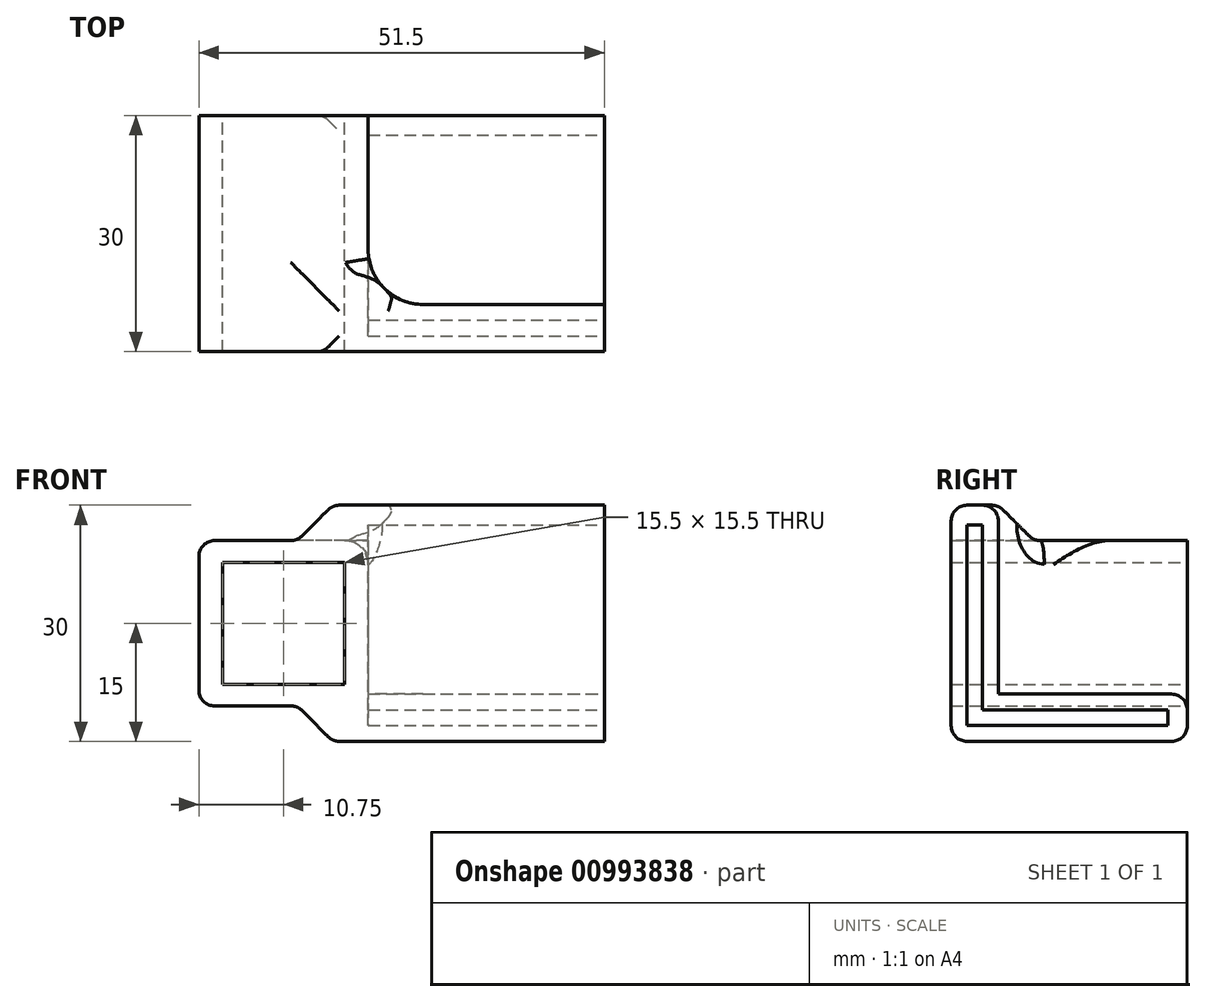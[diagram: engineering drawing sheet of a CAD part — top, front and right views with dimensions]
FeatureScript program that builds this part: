
annotation { "Feature Type Name" : "Feature", "Feature Type Description" : "" }
export const myFeature = defineFeature(function(context is Context, id is Id, definition is map)
    precondition{}
    {
        {
            var Q0;
            Q0=qCreatedBy(makeId("Top.planeOp"),FACE);
            var sketch = newSketch(context, id + "F0", { "sketchPlane" : qUnion([Q0])});
            skLineSegment(sketch, "E0", {"start": v(18, -44.27) * mm, "end": v(24, -44.27) * mm});
            skLineSegment(sketch, "E1", {"start": v(24, -44.27) * mm, "end": v(24, -14.27) * mm});
            skLineSegment(sketch, "E2", {"start": v(24, -14.27) * mm, "end": v(-12, -14.27) * mm});
            skLineSegment(sketch, "E3", {"start": v(-12, -14.27) * mm, "end": v(-12, -44.27) * mm});
            skLineSegment(sketch, "E4", {"start": v(-6, -44.27) * mm, "end": v(-6, -20.27) * mm});
            skLineSegment(sketch, "E5", {"start": v(-6, -20.27) * mm, "end": v(24, -20.27) * mm});
            skLineSegment(sketch, "E6", {"start": v(18, -44.27) * mm, "end": v(-12, -44.27) * mm});
            skSolve(sketch);
        }
        {
            var Q0;
            {var subQ2=sQuery(id+"F0.wireOp",EDGE,"E0");Q0=makeQuery(id+"F0.imprint","IMPRINT",FACE,{"disambiguationData":[TD([[makeQuery(id+"F0.imprint","IMPRINT",EDGE,{"derivedFrom":subQ2}),1.0]])]});}
            extrude(context, id + "F1", {"entities" : qUnion([Q0]), "depth" : 6 * mm, "offsetDistance" : 25 * mm});
        }
        {
            var Q0;
            {var subQ1=sQuery(id+"F0.wireOp",EDGE,"E2");Q0=makeQuery(id+"F0.imprint","IMPRINT",FACE,{"disambiguationData":[TD([[makeQuery(id+"F0.imprint","IMPRINT",EDGE,{"derivedFrom":subQ1}),1.0]])]});}
            extrude(context, id + "F2", {"entities" : qUnion([Q0]), "operationType" : NewBodyOperationType.ADD, "depth" : 30 * mm, "offsetDistance" : 25 * mm});
        }
        {
            var Q0;
            {var subQ0=sQuery(id+"F0.wireOp",EDGE,"E1");Q0=makeQuery(id+"F2.boolean.opBoolean","MERGE",FACE,{"derivedFrom":[makeQuery(id+"F1.opExtrude","SWEPT_FACE",FACE,{"disambiguationData":[OSD([subQ0])]}),makeQuery(id+"F2.opExtrude","SWEPT_FACE",FACE,{"disambiguationData":[OSD([subQ0])]})]});}
            var sketch = newSketch(context, id + "F3", { "sketchPlane" : qUnion([Q0])});
            skLineSegment(sketch, "E7", {"start": v(-41.77, 4) * mm, "end": v(-18.27, 4) * mm});
            skLineSegment(sketch, "E8", {"start": v(-18.27, 4) * mm, "end": v(-18.27, 27.5) * mm});
            skLineSegment(sketch, "E9", {"start": v(-18.27, 27.5) * mm, "end": v(-16.27, 27.5) * mm});
            skLineSegment(sketch, "E10", {"start": v(-16.27, 27.5) * mm, "end": v(-16.27, 2) * mm});
            skLineSegment(sketch, "E11", {"start": v(-16.27, 2) * mm, "end": v(-41.77, 2) * mm});
            skLineSegment(sketch, "E12", {"start": v(-41.77, 2) * mm, "end": v(-41.77, 4) * mm});
            skSolve(sketch);
        }
        {
            var Q0;
            Q0=makeQuery(id+"F3.imprint","IMPRINT",FACE,{"disambiguationData":[TD([[makeQuery(id+"F3.imprint","IMPRINT",EDGE,{"derivedFrom":sQuery(id+"F3.wireOp",EDGE,"E7")}),-1.0]])]});
            extrude(context, id + "F4", {"entities" : qUnion([Q0]), "operationType" : NewBodyOperationType.REMOVE, "oppositeDirection" : true, "depth" : 30 * mm, "offsetDistance" : 25 * mm});
        }
        {
            var Q0;
            Q0=makeQuery(id+"F2.opExtrude","SWEPT_FACE",FACE,{"disambiguationData":[OSD([sQuery(id+"F0.wireOp",EDGE,"E3")])]});
            extrude(context, id + "F5", {"entities" : qUnion([Q0]), "operationType" : NewBodyOperationType.ADD, "depth" : 20 * mm, "offsetDistance" : 25 * mm});
        }
        {
            var Q0;
            {var subQ0=sQuery(id+"F0.wireOp",EDGE,"E6");Q0=makeQuery(id+"F5.boolean.opBoolean","MERGE",FACE,{"derivedFrom":[makeQuery(id+"F2.boolean.opBoolean","MERGE",FACE,{"derivedFrom":[makeQuery(id+"F1.opExtrude","SWEPT_FACE",FACE,{"disambiguationData":[OSD([sQuery(id+"F0.wireOp",EDGE,"E0"),subQ0])]}),makeQuery(id+"F2.opExtrude","SWEPT_FACE",FACE,{"disambiguationData":[OSD([subQ0])]})]}),makeQuery(id+"F5.opExtrude","SWEPT_FACE",FACE,{"disambiguationData":[OSD([sQuery(id+"F0.wireOp",EDGE,"E3"),subQ0])]})]});}
            var sketch = newSketch(context, id + "F6", { "sketchPlane" : qUnion([Q0])});
            skLineSegment(sketch, "E13.bottom", {"start": v(-9, 7.25) * mm, "end": v(-24.5, 7.25) * mm});
            skLineSegment(sketch, "E13.top", {"start": v(-9, 22.75) * mm, "end": v(-24.5, 22.75) * mm});
            skLineSegment(sketch, "E13.left", {"start": v(-9, 7.25) * mm, "end": v(-9, 22.75) * mm});
            skLineSegment(sketch, "E13.right", {"start": v(-24.5, 7.25) * mm, "end": v(-24.5, 22.75) * mm});
            skPoint(sketch, "E13.middle", {"position": v(-16.75, 15) * mm});
            skLineSegment(sketch, "E14", {"start": v(-10.5, 25.5) * mm, "end": v(-10.5, 30) * mm});
            skLineSegment(sketch, "E15", {"start": v(-10.5, 25.5) * mm, "end": v(-27.5, 25.5) * mm});
            skLineSegment(sketch, "E16", {"start": v(-27.5, 25.5) * mm, "end": v(-27.5, 4.5) * mm});
            skLineSegment(sketch, "E17", {"start": v(-27.5, 4.5) * mm, "end": v(-10.5, 4.5) * mm});
            skLineSegment(sketch, "E18", {"start": v(-10.5, 4.5) * mm, "end": v(-10.5, 0) * mm});
            skLineSegment(sketch, "E19", {"start": v(-10.5, 0) * mm, "end": v(-32, 0) * mm});
            skLineSegment(sketch, "E20", {"start": v(-32, 0) * mm, "end": v(-32, 30) * mm});
            skLineSegment(sketch, "E21", {"start": v(-32, 30) * mm, "end": v(-10.5, 30) * mm});
            skLineSegment(sketch, "E22", {"start": v(-10.5, 25.5) * mm, "end": v(-6, 25.5) * mm});
            skLineSegment(sketch, "E23", {"start": v(-6, 25.5) * mm, "end": v(-6, 30) * mm});
            skLineSegment(sketch, "E24", {"start": v(-6, 30) * mm, "end": v(-10.5, 30) * mm});
            skSolve(sketch);
        }
        {
            var Q0;
            Q0=makeQuery(id+"F6.imprint","IMPRINT",FACE,{"disambiguationData":[TD([[makeQuery(id+"F6.imprint","IMPRINT",EDGE,{"derivedFrom":sQuery(id+"F6.wireOp",EDGE,"E13.bottom")}),-1.0]])]});
            var Q1;
            {var subQ0=sQuery(id+"F0.wireOp",EDGE,"E2");Q1=makeQuery(id+"F5.boolean.opBoolean","MERGE",FACE,{"derivedFrom":[makeQuery(id+"F2.opExtrude","SWEPT_FACE",FACE,{"disambiguationData":[OSD([subQ0])]}),makeQuery(id+"F5.opExtrude","SWEPT_FACE",FACE,{"disambiguationData":[OSD([subQ0,sQuery(id+"F0.wireOp",EDGE,"E3")])]})]});}
            extrude(context, id + "F7", {"entities" : qUnion([Q0]), "operationType" : NewBodyOperationType.REMOVE, "endBound" : BoundingType.UP_TO_SURFACE, "oppositeDirection" : true, "depth" : 25 * mm, "endBoundEntityFace" : qUnion([Q1]), "offsetDistance" : 25 * mm});
        }
        {
            var Q0;
            Q0=makeQuery(id+"F6.imprint","IMPRINT",FACE,{"disambiguationData":[TD([[makeQuery(id+"F6.imprint","IMPRINT",EDGE,{"derivedFrom":sQuery(id+"F6.wireOp",EDGE,"E14")}),1.0]])]});
            var Q1;
            {var subQ0=sQuery(id+"F0.wireOp",EDGE,"E2");Q1=makeQuery(id+"F5.boolean.opBoolean","MERGE",FACE,{"derivedFrom":[makeQuery(id+"F2.opExtrude","SWEPT_FACE",FACE,{"disambiguationData":[OSD([subQ0])]}),makeQuery(id+"F5.opExtrude","SWEPT_FACE",FACE,{"disambiguationData":[OSD([subQ0,sQuery(id+"F0.wireOp",EDGE,"E3")])]})]});}
            extrude(context, id + "F8", {"entities" : qUnion([Q0]), "operationType" : NewBodyOperationType.REMOVE, "endBound" : BoundingType.UP_TO_SURFACE, "oppositeDirection" : true, "depth" : 25 * mm, "endBoundEntityFace" : qUnion([Q1]), "offsetDistance" : 25 * mm});
        }
        {
            var Q0;
            Q0=makeQuery(id+"F6.imprint","IMPRINT",FACE,{"disambiguationData":[TD([[makeQuery(id+"F6.imprint","IMPRINT",EDGE,{"derivedFrom":sQuery(id+"F6.wireOp",EDGE,"E14")}),-1.0]])]});
            var Q1;
            Q1=makeQuery(id+"F2.opExtrude","SWEPT_FACE",FACE,{"disambiguationData":[OSD([sQuery(id+"F0.wireOp",EDGE,"E5")])]});
            extrude(context, id + "F9", {"entities" : qUnion([Q0]), "operationType" : NewBodyOperationType.REMOVE, "endBound" : BoundingType.UP_TO_SURFACE, "oppositeDirection" : true, "depth" : 22 * mm, "endBoundEntityFace" : qUnion([Q1]), "offsetDistance" : 25 * mm});
        }
        {
            var Q0;
            Q0=makeQuery(id+"F8.boolean.opBoolean","COPY",EDGE,{"derivedFrom":makeQuery(id+"F8.opExtrude","SWEPT_EDGE",EDGE,{"disambiguationData":[OSD([sQuery(id+"F6.wireOp",EDGE,"E14"),sQuery(id+"F6.wireOp",EDGE,"E15"),sQuery(id+"F6.wireOp",EDGE,"E22")])]})});
            var Q1;
            Q1=makeQuery(id+"F8.boolean.opBoolean","COPY",EDGE,{"derivedFrom":makeQuery(id+"F8.opExtrude","SWEPT_EDGE",EDGE,{"disambiguationData":[OSD([sQuery(id+"F6.wireOp",EDGE,"E17"),sQuery(id+"F6.wireOp",EDGE,"E18")])]})});
            var Q2;
            Q2=makeQuery(id+"F9.boolean.opBoolean","COPY",EDGE,{"derivedFrom":makeQuery(id+"F9.opExtrude","CAP_EDGE",EDGE,{"disambiguationData":[OSD([sQuery(id+"F6.wireOp",EDGE,"E22")])],"isStart":false})});
            chamfer(context, id + "F10", {"entities" : qUnion([Q0, Q1, Q2]), "width" : 4.5 * mm, "tangentPropagation" : true});
        }
        {
            var Q0;
            Q0=makeQuery(id+"F2.opExtrude","SWEPT_EDGE",EDGE,{"disambiguationData":[OSD([sQuery(id+"F0.wireOp",EDGE,"E4"),sQuery(id+"F0.wireOp",EDGE,"E5")])]});
            var Q1;
            Q1=makeQuery(id+"F1.opExtrude","CAP_EDGE",EDGE,{"disambiguationData":[OSD([sQuery(id+"F0.wireOp",EDGE,"E4")])],"isStart":false});
            var Q2;
            Q2=makeQuery(id+"F1.opExtrude","CAP_EDGE",EDGE,{"disambiguationData":[OSD([sQuery(id+"F0.wireOp",EDGE,"E5")])],"isStart":false});
            fillet(context, id + "F11", {"entities" : qUnion([Q0, Q1, Q2]), "radius" : 7 * mm, "tangentPropagation" : true, "allowEdgeOverflow" : false});
        }
        {
            var Q0;
            {var subQ0=sQuery(id+"F6.wireOp",EDGE,"E22");var subQ1=sQuery(id+"F6.wireOp",EDGE,"E15");Q0=makeQuery(id+"F10.opChamfer","BLEND_EDGE",EDGE,{"blendedFrom":[makeQuery(id+"F8.boolean.opBoolean","COPY",EDGE,{"derivedFrom":makeQuery(id+"F8.opExtrude","SWEPT_EDGE",EDGE,{"disambiguationData":[OSD([sQuery(id+"F6.wireOp",EDGE,"E14"),subQ1,subQ0])]})}),makeQuery(id+"F9.boolean.opBoolean","MERGE",FACE,{"derivedFrom":[makeQuery(id+"F8.boolean.opBoolean","COPY",FACE,{"derivedFrom":makeQuery(id+"F8.opExtrude","SWEPT_FACE",FACE,{"disambiguationData":[OSD([subQ1])]})})],"fromTools":[makeQuery(id+"F9.opExtrude","SWEPT_FACE",FACE,{"disambiguationData":[OSD([subQ0])]})]})],"blendedInto":[makeQuery(id+"F9.boolean.opBoolean","MERGE",FACE,{"derivedFrom":[makeQuery(id+"F8.boolean.opBoolean","COPY",FACE,{"derivedFrom":makeQuery(id+"F8.opExtrude","SWEPT_FACE",FACE,{"disambiguationData":[OSD([subQ1])]})})],"fromTools":[makeQuery(id+"F9.opExtrude","SWEPT_FACE",FACE,{"disambiguationData":[OSD([subQ0])]})]})]});}
            var Q1;
            {var subQ0=sQuery(id+"F6.wireOp",EDGE,"E22");Q1=makeQuery(id+"F10.opChamfer","BLEND_EDGE",EDGE,{"blendedFrom":[makeQuery(id+"F9.boolean.opBoolean","COPY",EDGE,{"derivedFrom":makeQuery(id+"F9.opExtrude","CAP_EDGE",EDGE,{"disambiguationData":[OSD([subQ0])],"isStart":false})}),makeQuery(id+"F9.boolean.opBoolean","MERGE",FACE,{"derivedFrom":[makeQuery(id+"F8.boolean.opBoolean","COPY",FACE,{"derivedFrom":makeQuery(id+"F8.opExtrude","SWEPT_FACE",FACE,{"disambiguationData":[OSD([sQuery(id+"F6.wireOp",EDGE,"E15")])]})})],"fromTools":[makeQuery(id+"F9.opExtrude","SWEPT_FACE",FACE,{"disambiguationData":[OSD([subQ0])]})]})],"blendedInto":[makeQuery(id+"F9.boolean.opBoolean","MERGE",FACE,{"derivedFrom":[makeQuery(id+"F8.boolean.opBoolean","COPY",FACE,{"derivedFrom":makeQuery(id+"F8.opExtrude","SWEPT_FACE",FACE,{"disambiguationData":[OSD([sQuery(id+"F6.wireOp",EDGE,"E15")])]})})],"fromTools":[makeQuery(id+"F9.opExtrude","SWEPT_FACE",FACE,{"disambiguationData":[OSD([subQ0])]})]})]});}
            var Q2;
            {var subQ0=sQuery(id+"F0.wireOp",EDGE,"E3");Q2=makeQuery(id+"F10.opChamfer","BLEND_EDGE",EDGE,{"blendedFrom":[makeQuery(id+"F9.boolean.opBoolean","COPY",EDGE,{"derivedFrom":makeQuery(id+"F9.opExtrude","CAP_EDGE",EDGE,{"disambiguationData":[OSD([sQuery(id+"F6.wireOp",EDGE,"E22")])],"isStart":false})}),makeQuery(id+"F5.boolean.opBoolean","MERGE",FACE,{"derivedFrom":[makeQuery(id+"F2.opExtrude","CAP_FACE",FACE,{"disambiguationData":[OSD([sQuery(id+"F0.wireOp",EDGE,"E1"),sQuery(id+"F0.wireOp",EDGE,"E2"),subQ0,sQuery(id+"F0.wireOp",EDGE,"E4"),sQuery(id+"F0.wireOp",EDGE,"E5"),sQuery(id+"F0.wireOp",EDGE,"E6")])],"isStart":false}),makeQuery(id+"F5.opExtrude","SWEPT_FACE",FACE,{"disambiguationData":[OSD([subQ0]),TDD([makeQuery(id+"F2.opExtrude","CAP_EDGE",EDGE,{"disambiguationData":[OSD([subQ0])],"isStart":false})])]})]})],"blendedInto":[makeQuery(id+"F5.boolean.opBoolean","MERGE",FACE,{"derivedFrom":[makeQuery(id+"F2.opExtrude","CAP_FACE",FACE,{"disambiguationData":[OSD([sQuery(id+"F0.wireOp",EDGE,"E1"),sQuery(id+"F0.wireOp",EDGE,"E2"),subQ0,sQuery(id+"F0.wireOp",EDGE,"E4"),sQuery(id+"F0.wireOp",EDGE,"E5"),sQuery(id+"F0.wireOp",EDGE,"E6")])],"isStart":false}),makeQuery(id+"F5.opExtrude","SWEPT_FACE",FACE,{"disambiguationData":[OSD([subQ0]),TDD([makeQuery(id+"F2.opExtrude","CAP_EDGE",EDGE,{"disambiguationData":[OSD([subQ0])],"isStart":false})])]})]})]});}
            var Q3;
            {var subQ0=sQuery(id+"F0.wireOp",EDGE,"E3");Q3=makeQuery(id+"F10.opChamfer","BLEND_EDGE",EDGE,{"blendedFrom":[makeQuery(id+"F8.boolean.opBoolean","COPY",EDGE,{"derivedFrom":makeQuery(id+"F8.opExtrude","SWEPT_EDGE",EDGE,{"disambiguationData":[OSD([sQuery(id+"F6.wireOp",EDGE,"E14"),sQuery(id+"F6.wireOp",EDGE,"E15"),sQuery(id+"F6.wireOp",EDGE,"E22")])]})}),makeQuery(id+"F5.boolean.opBoolean","MERGE",FACE,{"derivedFrom":[makeQuery(id+"F2.opExtrude","CAP_FACE",FACE,{"disambiguationData":[OSD([sQuery(id+"F0.wireOp",EDGE,"E1"),sQuery(id+"F0.wireOp",EDGE,"E2"),subQ0,sQuery(id+"F0.wireOp",EDGE,"E4"),sQuery(id+"F0.wireOp",EDGE,"E5"),sQuery(id+"F0.wireOp",EDGE,"E6")])],"isStart":false}),makeQuery(id+"F5.opExtrude","SWEPT_FACE",FACE,{"disambiguationData":[OSD([subQ0]),TDD([makeQuery(id+"F2.opExtrude","CAP_EDGE",EDGE,{"disambiguationData":[OSD([subQ0])],"isStart":false})])]})]})],"blendedInto":[makeQuery(id+"F5.boolean.opBoolean","MERGE",FACE,{"derivedFrom":[makeQuery(id+"F2.opExtrude","CAP_FACE",FACE,{"disambiguationData":[OSD([sQuery(id+"F0.wireOp",EDGE,"E1"),sQuery(id+"F0.wireOp",EDGE,"E2"),subQ0,sQuery(id+"F0.wireOp",EDGE,"E4"),sQuery(id+"F0.wireOp",EDGE,"E5"),sQuery(id+"F0.wireOp",EDGE,"E6")])],"isStart":false}),makeQuery(id+"F5.opExtrude","SWEPT_FACE",FACE,{"disambiguationData":[OSD([subQ0]),TDD([makeQuery(id+"F2.opExtrude","CAP_EDGE",EDGE,{"disambiguationData":[OSD([subQ0])],"isStart":false})])]})]})]});}
            var Q4;
            {var subQ0=sQuery(id+"F0.wireOp",EDGE,"E3");var subQ1=sQuery(id+"F0.wireOp",EDGE,"E2");Q4=makeQuery(id+"F5.boolean.opBoolean","MERGE",EDGE,{"derivedFrom":[makeQuery(id+"F2.opExtrude","CAP_EDGE",EDGE,{"disambiguationData":[OSD([subQ1])],"isStart":false}),makeQuery(id+"F5.opExtrude","SWEPT_EDGE",EDGE,{"disambiguationData":[OSD([subQ1,subQ0]),TDD([makeQuery(id+"F2.opExtrude","CAP_VERTEX",VERTEX,{"disambiguationData":[OSD([subQ1,subQ0])],"isStart":false})])]})]});}
            var Q5;
            Q5=makeQuery(id+"F9.boolean.opBoolean","MERGE",EDGE,{"derivedFrom":[makeQuery(id+"F2.opExtrude","CAP_EDGE",EDGE,{"disambiguationData":[OSD([sQuery(id+"F0.wireOp",EDGE,"E5")])],"isStart":false})],"fromTools":[makeQuery(id+"F9.opExtrude","CAP_EDGE",EDGE,{"disambiguationData":[OSD([sQuery(id+"F6.wireOp",EDGE,"E24")])],"isStart":false})]});
            var Q6;
            Q6=makeQuery(id+"F1.opExtrude","CAP_EDGE",EDGE,{"disambiguationData":[OSD([sQuery(id+"F0.wireOp",EDGE,"E0"),sQuery(id+"F0.wireOp",EDGE,"E6")])],"isStart":false});
            var Q7;
            Q7=makeQuery(id+"F8.boolean.opBoolean","COPY",EDGE,{"derivedFrom":makeQuery(id+"F8.opExtrude","SWEPT_EDGE",EDGE,{"disambiguationData":[OSD([sQuery(id+"F6.wireOp",EDGE,"E15"),sQuery(id+"F6.wireOp",EDGE,"E16")])]})});
            var Q8;
            Q8=makeQuery(id+"F8.boolean.opBoolean","COPY",EDGE,{"derivedFrom":makeQuery(id+"F8.opExtrude","SWEPT_EDGE",EDGE,{"disambiguationData":[OSD([sQuery(id+"F6.wireOp",EDGE,"E16"),sQuery(id+"F6.wireOp",EDGE,"E17")])]})});
            var Q9;
            {var subQ0=sQuery(id+"F0.wireOp",EDGE,"E3");var subQ1=sQuery(id+"F0.wireOp",EDGE,"E2");Q9=makeQuery(id+"F5.boolean.opBoolean","MERGE",EDGE,{"derivedFrom":[makeQuery(id+"F2.opExtrude","CAP_EDGE",EDGE,{"disambiguationData":[OSD([subQ1])],"isStart":true}),makeQuery(id+"F5.opExtrude","SWEPT_EDGE",EDGE,{"disambiguationData":[OSD([subQ1,subQ0]),TDD([makeQuery(id+"F2.opExtrude","CAP_VERTEX",VERTEX,{"disambiguationData":[OSD([subQ1,subQ0])],"isStart":true})])]})]});}
            var Q10;
            {var subQ0=sQuery(id+"F6.wireOp",EDGE,"E17");Q10=makeQuery(id+"F10.opChamfer","BLEND_EDGE",EDGE,{"blendedFrom":[makeQuery(id+"F8.boolean.opBoolean","COPY",EDGE,{"derivedFrom":makeQuery(id+"F8.opExtrude","SWEPT_EDGE",EDGE,{"disambiguationData":[OSD([subQ0,sQuery(id+"F6.wireOp",EDGE,"E18")])]})}),makeQuery(id+"F8.boolean.opBoolean","COPY",FACE,{"derivedFrom":makeQuery(id+"F8.opExtrude","SWEPT_FACE",FACE,{"disambiguationData":[OSD([subQ0])]})})],"blendedInto":[makeQuery(id+"F8.boolean.opBoolean","COPY",FACE,{"derivedFrom":makeQuery(id+"F8.opExtrude","SWEPT_FACE",FACE,{"disambiguationData":[OSD([subQ0])]})})]});}
            var Q11;
            {var subQ0=sQuery(id+"F0.wireOp",EDGE,"E6");var subQ1=sQuery(id+"F0.wireOp",EDGE,"E3");Q11=makeQuery(id+"F5.boolean.opBoolean","MERGE",EDGE,{"derivedFrom":[makeQuery(id+"F2.boolean.opBoolean","MERGE",EDGE,{"derivedFrom":[makeQuery(id+"F1.opExtrude","CAP_EDGE",EDGE,{"disambiguationData":[OSD([sQuery(id+"F0.wireOp",EDGE,"E0"),subQ0])],"isStart":true}),makeQuery(id+"F2.opExtrude","CAP_EDGE",EDGE,{"disambiguationData":[OSD([subQ0])],"isStart":true})]}),makeQuery(id+"F5.opExtrude","SWEPT_EDGE",EDGE,{"disambiguationData":[OSD([subQ1,subQ0]),TDD([makeQuery(id+"F2.opExtrude","CAP_VERTEX",VERTEX,{"disambiguationData":[OSD([subQ1,subQ0])],"isStart":true})])]})]});}
            var Q12;
            {var subQ0=sQuery(id+"F0.wireOp",EDGE,"E3");var subQ1=sQuery(id+"F0.wireOp",EDGE,"E6");var subQ2=sQuery(id+"F0.wireOp",EDGE,"E5");var subQ3=sQuery(id+"F0.wireOp",EDGE,"E4");var subQ4=sQuery(id+"F0.wireOp",EDGE,"E1");Q12=makeQuery(id+"F10.opChamfer","BLEND_EDGE",EDGE,{"blendedFrom":[makeQuery(id+"F8.boolean.opBoolean","COPY",EDGE,{"derivedFrom":makeQuery(id+"F8.opExtrude","SWEPT_EDGE",EDGE,{"disambiguationData":[OSD([sQuery(id+"F6.wireOp",EDGE,"E17"),sQuery(id+"F6.wireOp",EDGE,"E18")])]})}),makeQuery(id+"F5.boolean.opBoolean","MERGE",FACE,{"derivedFrom":[makeQuery(id+"F2.boolean.opBoolean","MERGE",FACE,{"derivedFrom":[makeQuery(id+"F1.opExtrude","CAP_FACE",FACE,{"disambiguationData":[OSD([sQuery(id+"F0.wireOp",EDGE,"E0"),subQ4,subQ3,subQ2,subQ1])],"isStart":true}),makeQuery(id+"F2.opExtrude","CAP_FACE",FACE,{"disambiguationData":[OSD([subQ4,sQuery(id+"F0.wireOp",EDGE,"E2"),subQ0,subQ3,subQ2,subQ1])],"isStart":true})]}),makeQuery(id+"F5.opExtrude","SWEPT_FACE",FACE,{"disambiguationData":[OSD([subQ0]),TDD([makeQuery(id+"F2.opExtrude","CAP_EDGE",EDGE,{"disambiguationData":[OSD([subQ0])],"isStart":true})])]})]})],"blendedInto":[makeQuery(id+"F5.boolean.opBoolean","MERGE",FACE,{"derivedFrom":[makeQuery(id+"F2.boolean.opBoolean","MERGE",FACE,{"derivedFrom":[makeQuery(id+"F1.opExtrude","CAP_FACE",FACE,{"disambiguationData":[OSD([sQuery(id+"F0.wireOp",EDGE,"E0"),subQ4,subQ3,subQ2,subQ1])],"isStart":true}),makeQuery(id+"F2.opExtrude","CAP_FACE",FACE,{"disambiguationData":[OSD([subQ4,sQuery(id+"F0.wireOp",EDGE,"E2"),subQ0,subQ3,subQ2,subQ1])],"isStart":true})]}),makeQuery(id+"F5.opExtrude","SWEPT_FACE",FACE,{"disambiguationData":[OSD([subQ0]),TDD([makeQuery(id+"F2.opExtrude","CAP_EDGE",EDGE,{"disambiguationData":[OSD([subQ0])],"isStart":true})])]})]})]});}
            fillet(context, id + "F12", {"entities" : qUnion([Q0, Q1, Q2, Q3, Q4, Q5, Q6, Q7, Q8, Q9, Q10, Q11, Q12]), "radius" : 2 * mm, "tangentPropagation" : true, "allowEdgeOverflow" : false});
        }
        {
            var Q0;
            Q0=makeQuery(id+"F9.boolean.opBoolean","COPY",EDGE,{"derivedFrom":makeQuery(id+"F9.opExtrude","SWEPT_EDGE",EDGE,{"disambiguationData":[OSD([sQuery(id+"F0.wireOp",EDGE,"E4"),sQuery(id+"F0.wireOp",EDGE,"E6"),sQuery(id+"F6.wireOp",EDGE,"E22"),sQuery(id+"F6.wireOp",EDGE,"E23")])]})});
            var Q1;
            Q1=makeQuery(id+"F11.opFillet","BLEND_EDGE",EDGE,{"blendedFrom":[makeQuery(id+"F2.opExtrude","SWEPT_EDGE",EDGE,{"disambiguationData":[OSD([sQuery(id+"F0.wireOp",EDGE,"E4"),sQuery(id+"F0.wireOp",EDGE,"E5")])]}),makeQuery(id+"F9.boolean.opBoolean","MERGE",FACE,{"derivedFrom":[makeQuery(id+"F8.boolean.opBoolean","COPY",FACE,{"derivedFrom":makeQuery(id+"F8.opExtrude","SWEPT_FACE",FACE,{"disambiguationData":[OSD([sQuery(id+"F6.wireOp",EDGE,"E15")])]})})],"fromTools":[makeQuery(id+"F9.opExtrude","SWEPT_FACE",FACE,{"disambiguationData":[OSD([sQuery(id+"F6.wireOp",EDGE,"E22")])]})]})],"blendedInto":[makeQuery(id+"F9.boolean.opBoolean","MERGE",FACE,{"derivedFrom":[makeQuery(id+"F8.boolean.opBoolean","COPY",FACE,{"derivedFrom":makeQuery(id+"F8.opExtrude","SWEPT_FACE",FACE,{"disambiguationData":[OSD([sQuery(id+"F6.wireOp",EDGE,"E15")])]})})],"fromTools":[makeQuery(id+"F9.opExtrude","SWEPT_FACE",FACE,{"disambiguationData":[OSD([sQuery(id+"F6.wireOp",EDGE,"E22")])]})]})]});
            var Q2;
            {var subQ0=sQuery(id+"F0.wireOp",EDGE,"E5");var subQ1=sQuery(id+"F0.wireOp",EDGE,"E4");var subQ2=sQuery(id+"F6.wireOp",EDGE,"E22");Q2=makeQuery(id+"F12.opFillet","BLEND_EDGE",EDGE,{"blendedFrom":[makeQuery(id+"F10.opChamfer","BLEND_EDGE",EDGE,{"blendedFrom":[makeQuery(id+"F9.boolean.opBoolean","COPY",EDGE,{"derivedFrom":makeQuery(id+"F9.opExtrude","CAP_EDGE",EDGE,{"disambiguationData":[OSD([subQ2])],"isStart":false})}),makeQuery(id+"F9.boolean.opBoolean","MERGE",FACE,{"derivedFrom":[makeQuery(id+"F8.boolean.opBoolean","COPY",FACE,{"derivedFrom":makeQuery(id+"F8.opExtrude","SWEPT_FACE",FACE,{"disambiguationData":[OSD([sQuery(id+"F6.wireOp",EDGE,"E15")])]})})],"fromTools":[makeQuery(id+"F9.opExtrude","SWEPT_FACE",FACE,{"disambiguationData":[OSD([subQ2])]})]})],"blendedInto":[makeQuery(id+"F9.boolean.opBoolean","MERGE",FACE,{"derivedFrom":[makeQuery(id+"F8.boolean.opBoolean","COPY",FACE,{"derivedFrom":makeQuery(id+"F8.opExtrude","SWEPT_FACE",FACE,{"disambiguationData":[OSD([sQuery(id+"F6.wireOp",EDGE,"E15")])]})})],"fromTools":[makeQuery(id+"F9.opExtrude","SWEPT_FACE",FACE,{"disambiguationData":[OSD([subQ2])]})]})]}),makeQuery(id+"F11.opFillet","BLEND_FACE",FACE,{"disambiguationData":[OSD([subQ1,subQ0]),TDD([makeQuery(id+"F2.opExtrude","SWEPT_EDGE",EDGE,{"disambiguationData":[OSD([subQ1,subQ0])]})])]})],"blendedInto":[makeQuery(id+"F11.opFillet","BLEND_FACE",FACE,{"disambiguationData":[OSD([subQ1,subQ0]),TDD([makeQuery(id+"F2.opExtrude","SWEPT_EDGE",EDGE,{"disambiguationData":[OSD([subQ1,subQ0])]})])]})]});}
            fillet(context, id + "F13", {"entities" : qUnion([Q0, Q1, Q2]), "radius" : 3 * mm, "allowEdgeOverflow" : false});
        }
        {
            var Q0;
            Q0=makeQuery(id+"F1.opExtrude","SWEPT_BODY",BODY,{"disambiguationData":[OSD([sQuery(id+"F0.wireOp",EDGE,"E0"),sQuery(id+"F0.wireOp",EDGE,"E1"),sQuery(id+"F0.wireOp",EDGE,"E4"),sQuery(id+"F0.wireOp",EDGE,"E5"),sQuery(id+"F0.wireOp",EDGE,"E6")])]});
            var Q1;
            Q1=qCreatedBy(makeId("Front.planeOp"),FACE);
            mirror(context, id + "F14", {"entities" : qUnion([Q0]), "mirrorPlane" : qUnion([Q1])});
        }
        {
            var Q0;
            Q0=makeQuery(id+"F1.opExtrude","SWEPT_BODY",BODY,{"disambiguationData":[OSD([sQuery(id+"F0.wireOp",EDGE,"E0"),sQuery(id+"F0.wireOp",EDGE,"E1"),sQuery(id+"F0.wireOp",EDGE,"E4"),sQuery(id+"F0.wireOp",EDGE,"E5"),sQuery(id+"F0.wireOp",EDGE,"E6")])]});
            deleteBodies(context, id + "F15", {"entities" : qUnion([Q0])});
        }
    });
